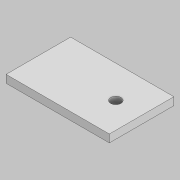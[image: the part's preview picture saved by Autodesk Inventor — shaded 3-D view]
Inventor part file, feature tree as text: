
AUTODESK INVENTOR PART (.ipt)
format: ipt  version: 2021 (Build 250183000, 183)  size: 83,968 bytes
history: native  units: mm
features: sketch x2, extrude x1, hole x1
ambient origin geometry x8: Origin, YZ Plane, XZ Plane, XY Plane, X Axis, Y Axis, Z Axis, Center Point
bodies: Solid1 (feature_tree)
feature tree (4):
  extrude  "base"  Depth=50.0mm
  hole  "mountingHole"  [1 undecoded]
  sketch  "Sketch1"  dims[d0=50.0mm d1=40.0mm]
  sketch  "Sketch2"  dims[d2=80.0mm d3=25.0mm d4=6.0mm d5=0.0mm d6=20.0mm d7=0.0mm d8=8.0mm d9=6.0mm d10=4.0mm d11=2.0mm d12=90.0deg d13=8.0mm d14=20.594885mm]
note: 1 required parameter value undecoded (feature->parameter linkage not recoverable at this tier; creation-order binding heuristic only, values carry confidence <= 0.55)
